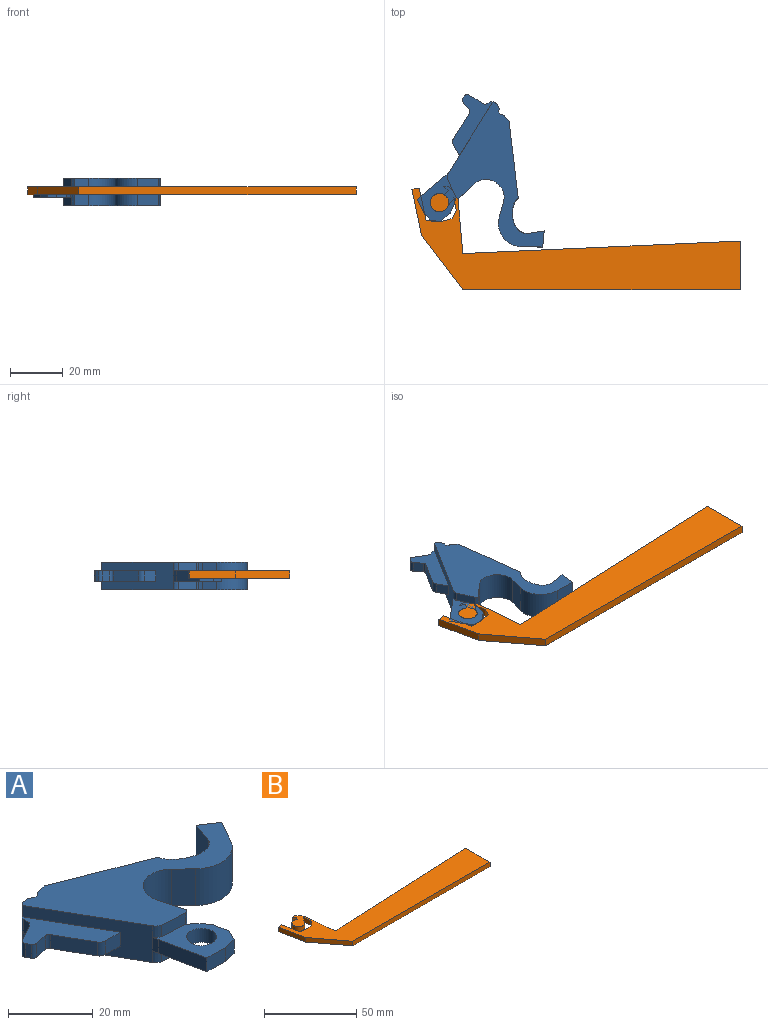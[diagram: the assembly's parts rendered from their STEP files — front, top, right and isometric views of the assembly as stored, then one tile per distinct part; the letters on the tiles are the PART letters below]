
ASSEMBLY  parts=2 mates=1
PART A: 46 faces, bbox 64.6x44.7x10.6 mm
  f0: plane 57.36x31.29mm, normal (0,0,1), area 690.7mm2, adj f1,f30,f31,f32,f33,f34,f35,f36
  f1: plane 10.6x6.98mm, normal (0.87,-0.48,0), area 84.5mm2, adj f0,f2,f32,f45
  f2: plane 57.36x31.29mm, normal (0,0,-1), area 690.7mm2, adj f1,f28,f29,f30,f31,f32,f33,f34
  f3: plane 4x0.97mm, normal (-0.9,0.45,0), area 4.3mm2, adj f4,f15,f16,f39
  f4: plane 4x2.05mm, normal (-1,0,0), area 8.2mm2, adj f3,f5,f15,f16
  f5: plane 4x0.99mm, normal (-0.65,0.76,0), area 5.2mm2, adj f4,f6,f15,f16
  f6: plane 5.22x4mm, normal (-0.5,0.87,0), area 24.1mm2, adj f5,f7,f15,f16
  f7: cylinder r=1.13mm len=4mm, axis (0,0,-1), area 7.1mm2, adj f6,f8,f15,f16
  f8: plane 4x1.12mm, normal (-0.87,-0.5,0), area 5.1mm2, adj f7,f9,f15,f16
  f9: cylinder r=1.13mm len=4mm, axis (0,0,-1), area 5.6mm2, adj f8,f10,f15,f16
  f10: plane 4x3.67mm, normal (0.19,-0.98,0), area 14.9mm2, adj f9,f11,f15,f16
  f11: cylinder r=1.13mm len=4mm, axis (0,0,-1), area 5.6mm2, adj f10,f12,f15,f16
  f12: plane 9.96x5.71mm, normal (-0.87,-0.5,0), area 45.9mm2, adj f11,f13,f15,f16
  f13: cylinder r=2.03mm len=4mm, axis (0,0,-1), area 8.5mm2, adj f12,f14,f15,f16
  f14: plane 4.92x4mm, normal (0,-1,0), area 19.7mm2, adj f13,f15,f16,f40
  f15: plane 20.87x19.22mm, normal (0,0,1), area 128.8mm2, adj f3,f4,f5,f6,f7,f8,f9,f10
  f16: plane 20.87x19.22mm, normal (0,0,-1), area 128.8mm2, adj f3,f4,f5,f6,f7,f8,f9,f10
  f17: plane 4x1.68mm, normal (-0.98,-0.2,0), area 6.8mm2, adj f18,f25,f26,f40
  f18: plane 13.36x4mm, normal (-0.98,-0.21,0), area 54.6mm2, adj f17,f19,f25,f26
  f19: plane 6.1x4mm, normal (-0.02,-1,0), area 24.4mm2, adj f18,f20,f25,f26
  f20: plane 4x3.75mm, normal (0.24,-0.97,0), area 15.4mm2, adj f19,f21,f25,f26
  f21: plane 4x3.16mm, normal (0.89,-0.46,0), area 14.2mm2, adj f20,f22,f25,f26
  f22: plane 4.74x4mm, normal (0.98,0.19,0), area 19.3mm2, adj f21,f25,f26,f27
  f23: cylinder r=3.5mm len=7mm, axis (0,0,-1), area 87.9mm2, adj f25,f26
  f24: plane 4x2.33mm, normal (0.62,0.78,0), area 11.9mm2, adj f25,f26,f27,f43
  f25: plane 15.16x14.62mm, normal (0,0,1), area 115.3mm2, adj f17,f18,f19,f20,f21,f22,f23,f24
  f26: plane 15.16x14.62mm, normal (0,0,-1), area 115.3mm2, adj f17,f18,f19,f20,f21,f22,f23,f24
  f27: plane 4x2.74mm, normal (0.79,0.61,0), area 13.9mm2, adj f22,f24,f25,f26
  f28: extruded ~3.3x1.63mm, area 7mm2, adj f2,f26,f29,f40
  f29: plane 7.63x3.3mm, normal (-0.06,-1,0), area 25.2mm2, adj f2,f26,f28,f43
  f30: cylinder r=6.84mm len=11.59mm, axis (0,0,-1), area 194.4mm2, adj f0,f2,f31,f44
  f31: plane 10.6x4.04mm, normal (-0.69,-0.72,0), area 59.5mm2, adj f0,f2,f30,f32
  f32: cylinder r=8.9mm len=13.96mm, axis (0,0,-1), area 172.9mm2, adj f0,f1,f2,f31
  f33: plane 10.6x6.6mm, normal (-0.94,0.33,0), area 74.2mm2, adj f0,f2,f34,f45
  f34: extruded ~13.21x10.6mm, area 175.6mm2, adj f0,f2,f33,f35
  f35: plane 27.32x10.62mm, normal (0.36,0.93,0), area 310.7mm2, adj f0,f2,f34,f36
  f36: extruded ~10.6x4.02mm, area 47.6mm2, adj f0,f2,f35,f37
  f37: plane 10.6x1.06mm, normal (-0.14,0.99,0), area 11.3mm2, adj f0,f2,f36,f38
  f38: plane 10.6x0.77mm, normal (0.68,0.74,0), area 11.1mm2, adj f0,f2,f37,f39
  f39: extruded ~10.6x3.57mm, area 40.9mm2, adj f0,f2,f3,f38,f40
  f40: plane 27.69x15.88mm, normal (-0.87,-0.5,0), area 242.1mm2, adj f0,f2,f14,f15,f16,f17,f28,f39
  f41: extruded ~3.3x1.63mm, area 7mm2, adj f0,f25,f40,f42
  f42: plane 7.63x3.3mm, normal (-0.06,-1,0), area 25.2mm2, adj f0,f25,f41,f43
  f43: extruded ~10.6x1.14mm, area 14.1mm2, adj f0,f2,f24,f29,f42,f44
  f44: plane 10.6x7.08mm, normal (0.96,0.27,0), area 77.9mm2, adj f0,f2,f30,f43
  f45: plane 10.6x5.08mm, normal (0.56,0.83,0), area 65mm2, adj f0,f1,f2,f33
PART B: 21 faces, bbox 124.3x39.1x3 mm
  f0: cylinder r=3.5mm len=7mm, axis (0,0,-1), area 52.1mm2, adj f1,f18,f19,f20
  f1: plane 3x3mm, normal (0.81,-0.58,0), area 11.1mm2, adj f0,f2,f19,f20
  f2: plane 4.74x3mm, normal (-0.98,-0.19,0), area 14.5mm2, adj f1,f3,f19,f20
  f3: plane 3.16x3mm, normal (-0.89,0.46,0), area 10.6mm2, adj f2,f4,f19,f20
  f4: plane 3.75x3mm, normal (-0.24,0.97,0), area 11.6mm2, adj f3,f5,f19,f20
  f5: plane 6.1x3mm, normal (0.02,1,0), area 18.3mm2, adj f4,f6,f19,f20
  f6: plane 12.21x3mm, normal (0.98,0.21,0), area 37.4mm2, adj f5,f7,f19,f20
  f7: plane 3x2.79mm, normal (-0.07,1,0), area 8.4mm2, adj f6,f8,f19,f20
  f8: plane 17.48x3.67mm, normal (-0.98,-0.21,0), area 53.6mm2, adj f7,f9,f19,f20
  f9: plane 20.62x15.63mm, normal (-0.8,-0.6,0), area 77.6mm2, adj f8,f10,f19,f20
  f10: plane 104.97x3mm, normal (0,-1,0), area 314.9mm2, adj f9,f11,f19,f20
  f11: plane 18.42x3mm, normal (1,0,0), area 55.3mm2, adj f10,f12,f19,f20
  f12: plane 104.97x4.74mm, normal (-0.05,1,0), area 315.2mm2, adj f11,f13,f19,f20
  f13: plane 20.77x3mm, normal (1,0.09,0), area 62.6mm2, adj f12,f14,f19,f20
  f14: plane 3x2.61mm, normal (0.89,0.45,0), area 8.7mm2, adj f13,f15,f19,f20
  f15: plane 3x2.34mm, normal (0.66,0.75,0), area 9.4mm2, adj f14,f16,f19,f20
  f16: plane 3x1.85mm, normal (-0.07,1,0), area 5.6mm2, adj f15,f17,f19,f20
  f17: plane 3x1.85mm, normal (-0.62,-0.78,0), area 7.1mm2, adj f16,f18,f19,f20
  f18: plane 3x1.66mm, normal (-0.78,0.62,0), area 6.4mm2, adj f0,f17,f19,f20
  f19: plane 124.27x39.13mm, normal (0,0,1), area 2031.4mm2, adj f0,f1,f2,f3,f4,f5,f6,f7
  f20: plane 124.27x39.13mm, normal (0,0,-1), area 2031.4mm2, adj f0,f1,f2,f3,f4,f5,f6,f7
PLACE A rot(axis=(0,0,-1),61.9deg) t=(146.79,113.08,-0.5)mm
PLACE B at identity fixed
MATE revolute A.f23 <-> B.f0  axis (0,0,-1) through (167.61,-65.76,1.5)mm
